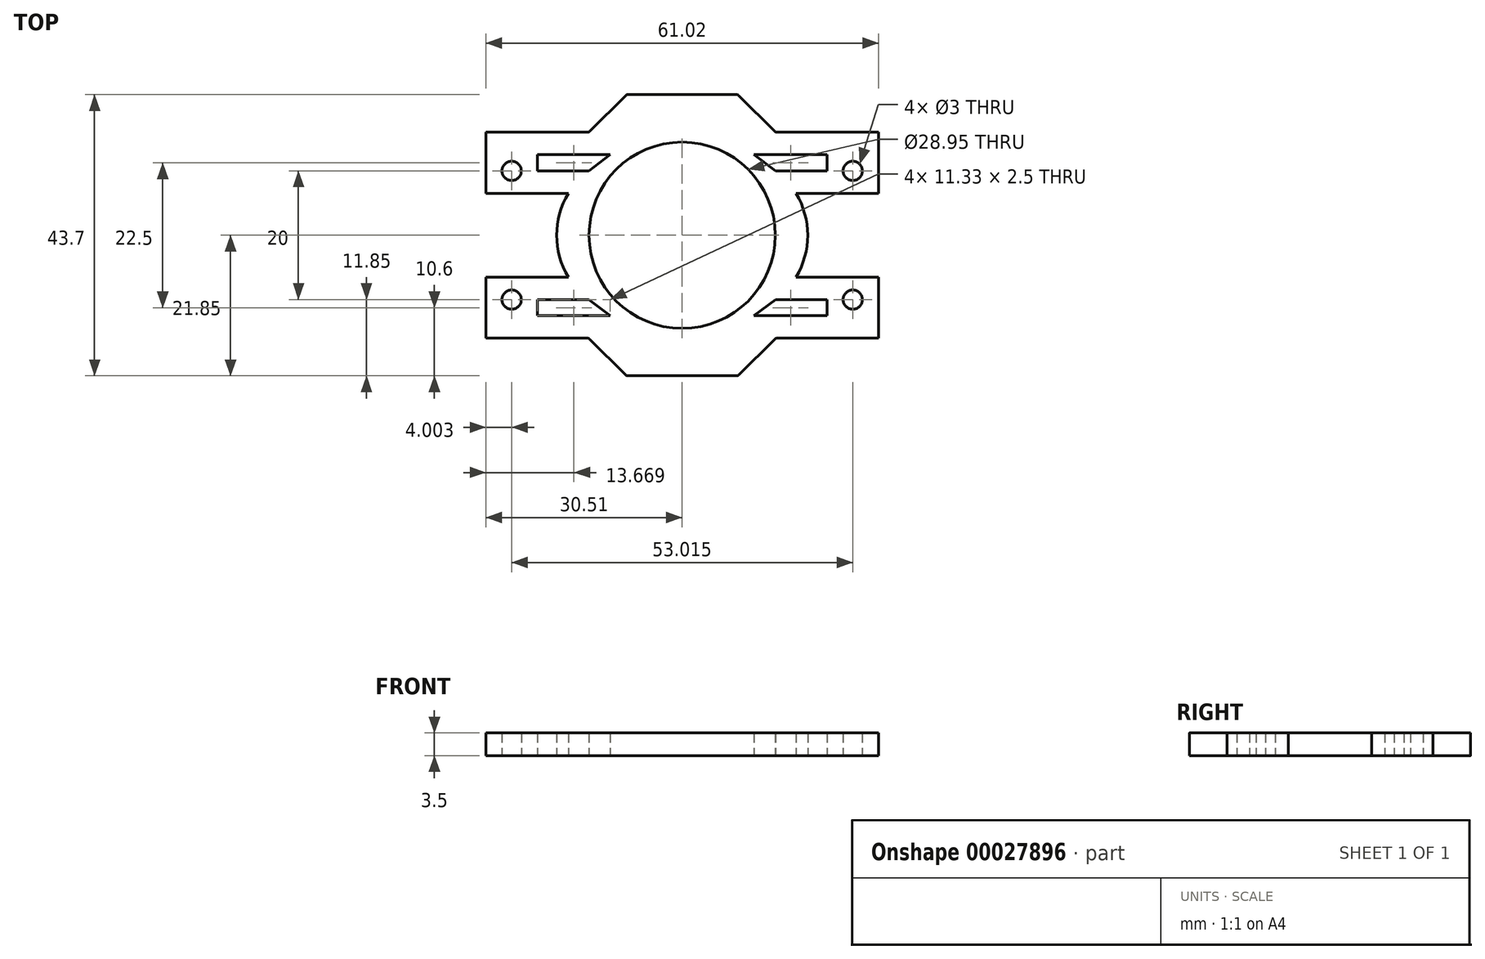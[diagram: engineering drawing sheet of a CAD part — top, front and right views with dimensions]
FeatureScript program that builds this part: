
annotation { "Feature Type Name" : "Feature", "Feature Type Description" : "" }
export const myFeature = defineFeature(function(context is Context, id is Id, definition is map)
    precondition{}
    {
        {
            var Q0;
            Q0=qCreatedBy(makeId("Top.planeOp"),FACE);
            var sketch = newSketch(context, id + "F0", { "sketchPlane" : qUnion([Q0])});
            skLineSegment(sketch, "E0.rect.bottom", {"start": v(30.5, 16) * mm, "end": v(-30.5, 16) * mm});
            skLineSegment(sketch, "E0.rect.top", {"start": v(30.5, -16) * mm, "end": v(-30.5, -16) * mm});
            skLineSegment(sketch, "E0.rect.left", {"start": v(30.5, 16) * mm, "end": v(30.5, -16) * mm});
            skLineSegment(sketch, "E0.rect.right", {"start": v(-30.5, 16) * mm, "end": v(-30.5, -16) * mm});
            skPoint(sketch, "E0.rect.middle", {"position": v(0, 0) * mm});
            skCircle(sketch, "E1", {"center": v(0, 0) * mm, "radius": 14.47 * mm});
            skLineSegment(sketch, "E2.rect.bottom", {"start": v(-19.5, -10) * mm, "end": v(-22.5, -10) * mm});
            skLineSegment(sketch, "E2.rect.top", {"start": v(-19.5, 10) * mm, "end": v(-22.5, 10) * mm});
            skLineSegment(sketch, "E2.rect.left", {"start": v(-19.5, -10) * mm, "end": v(-19.5, 10) * mm});
            skLineSegment(sketch, "E2.rect.right", {"start": v(-22.5, -10) * mm, "end": v(-22.5, 10) * mm});
            skPoint(sketch, "E2.rect.middle", {"position": v(-21, 0) * mm});
            skLineSegment(sketch, "E3.MirrorCS", {"start": v(19.5, 10) * mm, "end": v(22.5, 10) * mm});
            skLineSegment(sketch, "E4.MirrorCS", {"start": v(22.5, -10) * mm, "end": v(22.5, 10) * mm});
            skLineSegment(sketch, "E5.MirrorCS", {"start": v(19.5, -10) * mm, "end": v(22.5, -10) * mm});
            skLineSegment(sketch, "E6.MirrorCS", {"start": v(19.5, -10) * mm, "end": v(19.5, 10) * mm});
            skCircle(sketch, "E7", {"center": v(-26.5, 10) * mm, "radius": 1.5 * mm});
            skCircle(sketch, "E8", {"center": v(-26.5, -10) * mm, "radius": 1.5 * mm});
            skCircle(sketch, "E9.MirrorC", {"center": v(26.5, 10) * mm, "radius": 1.5 * mm});
            skCircle(sketch, "E10.MirrorC", {"center": v(26.5, -10) * mm, "radius": 1.5 * mm});
            skLineSegment(sketch, "E11", {"start": v(-19.5, -10) * mm, "end": v(-14.5, -10) * mm});
            skLineSegment(sketch, "E12", {"start": v(-19.5, 10) * mm, "end": v(-14.5, 10) * mm});
            skArc(sketch, "E13", {"start": v(-14.5, 10) * mm, "mid": v(-19.5, 0) * mm, "end": v(-14.5, -10) * mm});
            skArc(sketch, "E14.MirrorCS", {"start": v(14.5, 10) * mm, "mid": v(19.5, 0) * mm, "end": v(14.5, -10) * mm});
            skLineSegment(sketch, "E15.MirrorCS", {"start": v(19.5, -10) * mm, "end": v(14.5, -10) * mm});
            skLineSegment(sketch, "E16.MirrorCS", {"start": v(19.5, 10) * mm, "end": v(14.5, 10) * mm});
            skLineSegment(sketch, "E17", {"start": v(-22.5, 6.5) * mm, "end": v(-19.5, 6.5) * mm});
            skLineSegment(sketch, "E18", {"start": v(-22.5, -6.5) * mm, "end": v(-19.5, -6.5) * mm});
            skLineSegment(sketch, "E19", {"start": v(-19.5, -6.5) * mm, "end": v(-17.69, -6.5) * mm});
            skLineSegment(sketch, "E20", {"start": v(-19.5, 6.5) * mm, "end": v(-17.69, 6.5) * mm});
            skLineSegment(sketch, "E21.bottom", {"start": v(-22.5, 6.5) * mm, "end": v(-30.5, 6.5) * mm});
            skLineSegment(sketch, "E21.top", {"start": v(-22.5, -6.5) * mm, "end": v(-30.5, -6.5) * mm});
            skLineSegment(sketch, "E21.left", {"start": v(-22.5, 6.5) * mm, "end": v(-22.5, -6.5) * mm});
            skLineSegment(sketch, "E21.right", {"start": v(-30.5, 6.5) * mm, "end": v(-30.5, -6.5) * mm});
            skLineSegment(sketch, "E22.MirrorCS", {"start": v(19.5, 6.5) * mm, "end": v(17.69, 6.5) * mm});
            skLineSegment(sketch, "E23.MirrorCS", {"start": v(22.5, 6.5) * mm, "end": v(19.5, 6.5) * mm});
            skLineSegment(sketch, "E24.MirrorCS", {"start": v(22.5, 6.5) * mm, "end": v(30.5, 6.5) * mm});
            skLineSegment(sketch, "E25.MirrorCS", {"start": v(22.5, -6.5) * mm, "end": v(30.5, -6.5) * mm});
            skLineSegment(sketch, "E26.MirrorCS", {"start": v(22.5, -6.5) * mm, "end": v(19.5, -6.5) * mm});
            skLineSegment(sketch, "E27.MirrorCS", {"start": v(19.5, -6.5) * mm, "end": v(17.69, -6.5) * mm});
            skLineSegment(sketch, "E28", {"start": v(-14.5, -16) * mm, "end": v(-8.66, -21.85) * mm});
            skLineSegment(sketch, "E29", {"start": v(-8.66, -21.85) * mm, "end": v(8.66, -21.85) * mm});
            skLineSegment(sketch, "E30", {"start": v(8.66, -21.85) * mm, "end": v(14.5, -16) * mm});
            skLineSegment(sketch, "E31.MirrorCS", {"start": v(-8.66, -21.85) * mm, "end": v(-8.66, -39.17) * mm});
            skLineSegment(sketch, "E32.MirrorCS", {"start": v(-14.5, 16) * mm, "end": v(-8.66, 21.85) * mm});
            skLineSegment(sketch, "E33.MirrorCS", {"start": v(-8.66, 21.85) * mm, "end": v(8.66, 21.85) * mm});
            skLineSegment(sketch, "E34.MirrorCS", {"start": v(8.66, 21.85) * mm, "end": v(14.5, 16) * mm});
            skLineSegment(sketch, "E35.bottom", {"start": v(-14.5, -10) * mm, "end": v(-22.5, -10) * mm});
            skLineSegment(sketch, "E35.top", {"start": v(-14.5, -12.5) * mm, "end": v(-22.5, -12.5) * mm});
            skLineSegment(sketch, "E35.left", {"start": v(-14.5, -10) * mm, "end": v(-14.5, -12.5) * mm});
            skLineSegment(sketch, "E35.right", {"start": v(-22.5, -10) * mm, "end": v(-22.5, -12.5) * mm});
            skLineSegment(sketch, "E36", {"start": v(30.5, 0) * mm, "end": v(-30.5, 0) * mm, "construction": true});
            skLineSegment(sketch, "E37", {"start": v(0, -21.85) * mm, "end": v(0, 21.85) * mm, "construction": true});
            skLineSegment(sketch, "E38.MirrorCS", {"start": v(-14.5, 12.5) * mm, "end": v(-22.5, 12.5) * mm});
            skLineSegment(sketch, "E39.MirrorCS", {"start": v(-22.5, 10) * mm, "end": v(-22.5, 12.5) * mm});
            skLineSegment(sketch, "E40.MirrorCS", {"start": v(-14.5, 10) * mm, "end": v(-14.5, 12.5) * mm});
            skLineSegment(sketch, "E41.MirrorCS", {"start": v(-45.02, -21.85) * mm, "end": v(-45.02, 21.85) * mm});
            skLineSegment(sketch, "E42.MirrorCS", {"start": v(14.5, 10) * mm, "end": v(14.5, 12.5) * mm});
            skLineSegment(sketch, "E43.MirrorCS", {"start": v(14.5, 12.5) * mm, "end": v(22.5, 12.5) * mm});
            skLineSegment(sketch, "E44.MirrorCS", {"start": v(22.5, 10) * mm, "end": v(22.5, 12.5) * mm});
            skLineSegment(sketch, "E45.MirrorCS", {"start": v(22.5, -10) * mm, "end": v(22.5, -12.5) * mm});
            skLineSegment(sketch, "E46.MirrorCS", {"start": v(14.5, -12.5) * mm, "end": v(22.5, -12.5) * mm});
            skLineSegment(sketch, "E47.MirrorCS", {"start": v(14.5, -10) * mm, "end": v(14.5, -12.5) * mm});
            skLineSegment(sketch, "E48", {"start": v(-14.5, -12.5) * mm, "end": v(-12, -12.5) * mm});
            skLineSegment(sketch, "E49", {"start": v(-14.5, -10) * mm, "end": v(-11.18, -12.5) * mm});
            skLineSegment(sketch, "E50", {"start": v(-11.18, -12.5) * mm, "end": v(-12, -12.5) * mm});
            skLineSegment(sketch, "E51.MirrorCS", {"start": v(14.5, -12.5) * mm, "end": v(12, -12.5) * mm});
            skLineSegment(sketch, "E52.MirrorCS", {"start": v(11.18, -12.5) * mm, "end": v(12, -12.5) * mm});
            skLineSegment(sketch, "E53.MirrorCS", {"start": v(14.5, -10) * mm, "end": v(11.18, -12.5) * mm});
            skLineSegment(sketch, "E54.MirrorCS", {"start": v(14.5, 12.5) * mm, "end": v(12, 12.5) * mm});
            skLineSegment(sketch, "E55.MirrorCS", {"start": v(11.18, 12.5) * mm, "end": v(12, 12.5) * mm});
            skLineSegment(sketch, "E56.MirrorCS", {"start": v(14.5, 10) * mm, "end": v(11.18, 12.5) * mm});
            skLineSegment(sketch, "E57.MirrorCS", {"start": v(-14.5, 12.5) * mm, "end": v(-12, 12.5) * mm});
            skLineSegment(sketch, "E58.MirrorCS", {"start": v(-11.18, 12.5) * mm, "end": v(-12, 12.5) * mm});
            skLineSegment(sketch, "E59.MirrorCS", {"start": v(-14.5, 10) * mm, "end": v(-11.18, 12.5) * mm});
            skSolve(sketch);
        }
        {
            var Q0;
            Q0=makeQuery(id+"F0.imprint","IMPRINT",FACE,{"disambiguationData":[TD([[makeQuery(id+"F0.imprint","IMPRINT",EDGE,{"derivedFrom":sQuery(id+"F0.wireOp",EDGE,"E0.rect.bottom")}),1.0]])]});
            var Q1;
            {var subQ2=sQuery(id+"F0.wireOp",EDGE,"E2.rect.top");Q1=makeQuery(id+"F0.imprint","IMPRINT",FACE,{"disambiguationData":[TD([[makeQuery(id+"F0.imprint","IMPRINT",EDGE,{"derivedFrom":subQ2}),1.0]])]});}
            var Q2;
            {var subQ2=sQuery(id+"F0.wireOp",EDGE,"E12");Q2=makeQuery(id+"F0.imprint","IMPRINT",FACE,{"disambiguationData":[TD([[makeQuery(id+"F0.imprint","IMPRINT",EDGE,{"derivedFrom":subQ2}),-1.0]])]});}
            var Q3;
            {var subQ2=sQuery(id+"F0.wireOp",EDGE,"E2.rect.bottom");Q3=makeQuery(id+"F0.imprint","IMPRINT",FACE,{"disambiguationData":[TD([[makeQuery(id+"F0.imprint","IMPRINT",EDGE,{"derivedFrom":subQ2}),-1.0]])]});}
            var Q4;
            {var subQ2=sQuery(id+"F0.wireOp",EDGE,"E11");Q4=makeQuery(id+"F0.imprint","IMPRINT",FACE,{"disambiguationData":[TD([[makeQuery(id+"F0.imprint","IMPRINT",EDGE,{"derivedFrom":subQ2}),1.0]])]});}
            var Q5;
            {var subQ2=sQuery(id+"F0.wireOp",EDGE,"E16.MirrorCS");Q5=makeQuery(id+"F0.imprint","IMPRINT",FACE,{"disambiguationData":[TD([[makeQuery(id+"F0.imprint","IMPRINT",EDGE,{"derivedFrom":subQ2}),1.0]])]});}
            var Q6;
            {var subQ2=sQuery(id+"F0.wireOp",EDGE,"E3.MirrorCS");Q6=makeQuery(id+"F0.imprint","IMPRINT",FACE,{"disambiguationData":[TD([[makeQuery(id+"F0.imprint","IMPRINT",EDGE,{"derivedFrom":subQ2}),-1.0]])]});}
            var Q7;
            {var subQ1=sQuery(id+"F0.wireOp",EDGE,"E15.MirrorCS");Q7=makeQuery(id+"F0.imprint","IMPRINT",FACE,{"disambiguationData":[TD([[makeQuery(id+"F0.imprint","IMPRINT",EDGE,{"derivedFrom":subQ1}),-1.0]])]});}
            var Q8;
            {var subQ2=sQuery(id+"F0.wireOp",EDGE,"E5.MirrorCS");Q8=makeQuery(id+"F0.imprint","IMPRINT",FACE,{"disambiguationData":[TD([[makeQuery(id+"F0.imprint","IMPRINT",EDGE,{"derivedFrom":subQ2}),1.0]])]});}
            var Q9;
            {var subQ1=sQuery(id+"F0.wireOp",EDGE,"E28");Q9=makeQuery(id+"F0.imprint","IMPRINT",FACE,{"disambiguationData":[TD([[makeQuery(id+"F0.imprint","IMPRINT",EDGE,{"derivedFrom":subQ1}),1.0]])]});}
            var Q10;
            {var subQ1=sQuery(id+"F0.wireOp",EDGE,"E32.MirrorCS");Q10=makeQuery(id+"F0.imprint","IMPRINT",FACE,{"disambiguationData":[TD([[makeQuery(id+"F0.imprint","IMPRINT",EDGE,{"derivedFrom":subQ1}),-1.0]])]});}
            var Q11;
            {var subQ5=sQuery(id+"F0.wireOp",EDGE,"E18");Q11=makeQuery(id+"F0.imprint","IMPRINT",FACE,{"disambiguationData":[TD([[makeQuery(id+"F0.imprint","IMPRINT",EDGE,{"derivedFrom":subQ5}),-1.0]])]});}
            var Q12;
            {var subQ5=sQuery(id+"F0.wireOp",EDGE,"E19");Q12=makeQuery(id+"F0.imprint","IMPRINT",FACE,{"disambiguationData":[TD([[makeQuery(id+"F0.imprint","IMPRINT",EDGE,{"derivedFrom":subQ5}),-1.0]])]});}
            extrude(context, id + "F1", {"entities" : qUnion([Q0, Q1, Q2, Q3, Q4, Q5, Q6, Q7, Q8, Q9, Q10, Q11, Q12]), "depth" : 3.5 * mm});
        }
        {
            var Q0;
            Q0=makeQuery(id+"F1.opExtrude","SWEPT_EDGE",EDGE,{"disambiguationData":[OSD([sQuery(id+"F0.wireOp",EDGE,"E29"),sQuery(id+"F0.wireOp",EDGE,"E30")])]});
            var Q1;
            Q1=makeQuery(id+"F1.opExtrude","SWEPT_EDGE",EDGE,{"disambiguationData":[OSD([sQuery(id+"F0.wireOp",EDGE,"E28"),sQuery(id+"F0.wireOp",EDGE,"E29")])]});
            var Q2;
            Q2=makeQuery(id+"F1.opExtrude","SWEPT_EDGE",EDGE,{"disambiguationData":[OSD([sQuery(id+"F0.wireOp",EDGE,"E0.rect.top"),sQuery(id+"F0.wireOp",EDGE,"E30")])]});
            var Q3;
            Q3=makeQuery(id+"F1.opExtrude","SWEPT_EDGE",EDGE,{"disambiguationData":[OSD([sQuery(id+"F0.wireOp",EDGE,"E0.rect.top"),sQuery(id+"F0.wireOp",EDGE,"E28")])]});
            var Q4;
            Q4=makeQuery(id+"F1.opExtrude","SWEPT_EDGE",EDGE,{"disambiguationData":[OSD([sQuery(id+"F0.wireOp",EDGE,"E0.rect.bottom"),sQuery(id+"F0.wireOp",EDGE,"E34.MirrorCS")])]});
            var Q5;
            Q5=makeQuery(id+"F1.opExtrude","SWEPT_EDGE",EDGE,{"disambiguationData":[OSD([sQuery(id+"F0.wireOp",EDGE,"E33.MirrorCS"),sQuery(id+"F0.wireOp",EDGE,"E34.MirrorCS")])]});
            var Q6;
            Q6=makeQuery(id+"F1.opExtrude","SWEPT_EDGE",EDGE,{"disambiguationData":[OSD([sQuery(id+"F0.wireOp",EDGE,"E32.MirrorCS"),sQuery(id+"F0.wireOp",EDGE,"E33.MirrorCS")])]});
            var Q7;
            Q7=makeQuery(id+"F1.opExtrude","SWEPT_EDGE",EDGE,{"disambiguationData":[OSD([sQuery(id+"F0.wireOp",EDGE,"E0.rect.bottom"),sQuery(id+"F0.wireOp",EDGE,"E32.MirrorCS")])]});
            fillet(context, id + "F2", {"entities" : qUnion([Q0, Q1, Q2, Q3, Q4, Q5, Q6, Q7]), "radius" : .5 * mm, "tangentPropagation" : true, "allowEdgeOverflow" : false});
        }
    });
